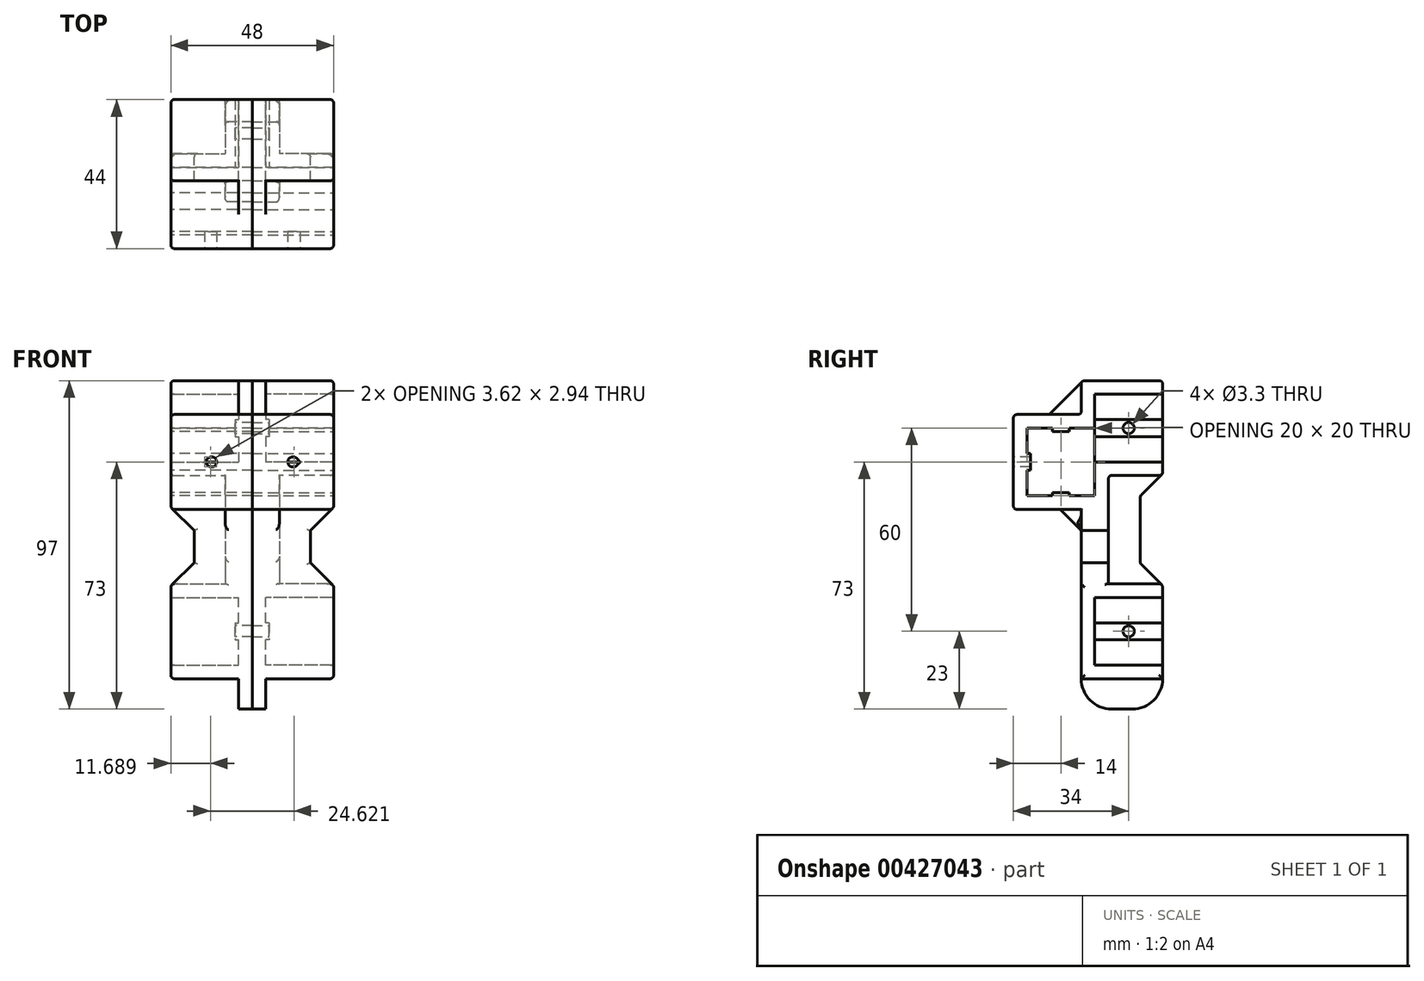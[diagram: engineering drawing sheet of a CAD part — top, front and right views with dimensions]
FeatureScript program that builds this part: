
annotation { "Feature Type Name" : "Feature", "Feature Type Description" : "" }
export const myFeature = defineFeature(function(context is Context, id is Id, definition is map)
    precondition{}
    {
        {
            var Q0;
            Q0=qCreatedBy(makeId("Right.planeOp"),FACE);
            var sketch = newSketch(context, id + "F0", { "sketchPlane" : qUnion([Q0])});
            skLineSegment(sketch, "E0", {"start": v(-23, 24) * mm, "end": v(-1, 24) * mm});
            skLineSegment(sketch, "E1", {"start": v(0, 23) * mm, "end": v(0, 20) * mm});
            skLineSegment(sketch, "E2", {"start": v(-1, -4) * mm, "end": v(-15, -4) * mm});
            skLineSegment(sketch, "E3", {"start": v(-16, -5) * mm, "end": v(-16, -14) * mm});
            skLineSegment(sketch, "E4", {"start": v(-16, -14) * mm, "end": v(-43, -14) * mm});
            skLineSegment(sketch, "E5", {"start": v(-44, -13) * mm, "end": v(-44, 13) * mm});
            skLineSegment(sketch, "E6", {"start": v(-43, 14) * mm, "end": v(-33.83, 14) * mm});
            skLineSegment(sketch, "E7", {"start": v(-24, 15) * mm, "end": v(-24, 23) * mm});
            skLineSegment(sketch, "E8", {"start": v(-23.7, 23.7) * mm, "end": v(-33.12, 14.3) * mm});
            skLineSegment(sketch, "E9", {"start": v(0, 20) * mm, "end": v(-20, 20) * mm});
            skLineSegment(sketch, "E10", {"start": v(-20, 20) * mm, "end": v(-20, 10) * mm});
            skLineSegment(sketch, "E11", {"start": v(-20, 10) * mm, "end": v(-27.5, 10) * mm});
            skLineSegment(sketch, "E12", {"start": v(-27.5, 10) * mm, "end": v(-27.5, 9) * mm});
            skLineSegment(sketch, "E13", {"start": v(-27.5, 9) * mm, "end": v(-32.5, 9) * mm});
            skLineSegment(sketch, "E14", {"start": v(-32.5, 9) * mm, "end": v(-32.5, 10) * mm});
            skLineSegment(sketch, "E15", {"start": v(-32.5, 10) * mm, "end": v(-40, 10) * mm});
            skLineSegment(sketch, "E16", {"start": v(-40, 10) * mm, "end": v(-40, 2.5) * mm});
            skLineSegment(sketch, "E17", {"start": v(-40, 2.5) * mm, "end": v(-39, 2.5) * mm});
            skLineSegment(sketch, "E18", {"start": v(-39, 2.5) * mm, "end": v(-39, -2.5) * mm});
            skLineSegment(sketch, "E19", {"start": v(-39, -2.5) * mm, "end": v(-40, -2.5) * mm});
            skLineSegment(sketch, "E20", {"start": v(-40, -2.5) * mm, "end": v(-40, -10) * mm});
            skLineSegment(sketch, "E21", {"start": v(-40, -10) * mm, "end": v(-32.5, -10) * mm});
            skLineSegment(sketch, "E22", {"start": v(-32.5, -10) * mm, "end": v(-32.5, -9) * mm});
            skLineSegment(sketch, "E23", {"start": v(-32.5, -9) * mm, "end": v(-27.5, -9) * mm});
            skLineSegment(sketch, "E24", {"start": v(-27.5, -9) * mm, "end": v(-27.5, -10) * mm});
            skLineSegment(sketch, "E25", {"start": v(-27.5, -10) * mm, "end": v(-20, -10) * mm});
            skLineSegment(sketch, "E26", {"start": v(-20, -10) * mm, "end": v(-20, 0) * mm});
            skLineSegment(sketch, "E27", {"start": v(-20, 0) * mm, "end": v(0, 0) * mm});
            skPoint(sketch, "E28.visualSharp", {"position": v(-44, 14) * mm});
            skArc(sketch, "E28.filletArc", {"start": v(-43, 14) * mm, "mid": v(-43.7, 13.7) * mm, "end": v(-44, 13) * mm});
            skPoint(sketch, "E29.visualSharp", {"position": v(-44, -14) * mm});
            skArc(sketch, "E29.filletArc", {"start": v(-44, -13) * mm, "mid": v(-43.7, -13.7) * mm, "end": v(-43, -14) * mm});
            skPoint(sketch, "E30.visualSharp", {"position": v(-16, -4) * mm});
            skArc(sketch, "E30.filletArc", {"start": v(-15, -4) * mm, "mid": v(-15.7, -4.3) * mm, "end": v(-16, -5) * mm});
            skPoint(sketch, "E31.visualSharp", {"position": v(0, 24) * mm});
            skArc(sketch, "E31.filletArc", {"start": v(0, 23) * mm, "mid": v(-0.3, 23.7) * mm, "end": v(-1, 24) * mm});
            skArc(sketch, "E32.filletArc", {"start": v(-23, 24) * mm, "mid": v(-23.7, 23.7) * mm, "end": v(-24, 23) * mm});
            skPoint(sketch, "E33.visualSharp", {"position": v(-24, 14) * mm});
            skArc(sketch, "E33.filletArc", {"start": v(-25, 14) * mm, "mid": v(-24.3, 14.3) * mm, "end": v(-24, 15) * mm});
            skLineSegment(sketch, "E34", {"start": v(-20, 0) * mm, "end": v(-20, 10) * mm});
            skLineSegment(sketch, "E35", {"start": v(0, 20) * mm, "end": v(0, 0) * mm});
            skArc(sketch, "E36.filletArc", {"start": v(-33.83, 14) * mm, "mid": v(-33.45, 14.08) * mm, "end": v(-33.12, 14.3) * mm});
            skLineSegment(sketch, "E37", {"start": v(-33.83, 14) * mm, "end": v(-25, 14) * mm});
            skLineSegment(sketch, "E38", {"start": v(-24, -64) * mm, "end": v(-24, -14) * mm});
            skLineSegment(sketch, "E39", {"start": v(0, -64) * mm, "end": v(0, -60) * mm});
            skLineSegment(sketch, "E40", {"start": v(0, -60) * mm, "end": v(-20, -60) * mm});
            skLineSegment(sketch, "E41", {"start": v(-20, -60) * mm, "end": v(-20, -40) * mm});
            skLineSegment(sketch, "E42", {"start": v(-20, -40) * mm, "end": v(0, -40) * mm});
            skLineSegment(sketch, "E43", {"start": v(0, -40) * mm, "end": v(0, -37) * mm});
            skLineSegment(sketch, "E44", {"start": v(-24, -64) * mm, "end": v(0, -64) * mm});
            skLineSegment(sketch, "E45", {"start": v(0, -60) * mm, "end": v(0, -40) * mm});
            skLineSegment(sketch, "E46", {"start": v(-1, -36) * mm, "end": v(-24, -36) * mm});
            skLineSegment(sketch, "E47", {"start": v(-16, -14) * mm, "end": v(-16, -36) * mm});
            skLineSegment(sketch, "E48", {"start": v(-30.27, -14) * mm, "end": v(-24, -20.27) * mm});
            skLineSegment(sketch, "E49", {"start": v(-6.56, -9.97) * mm, "end": v(-0.3, -3.7) * mm});
            skLineSegment(sketch, "E50", {"start": v(-6.56, -30.03) * mm, "end": v(-0.3, -36.3) * mm});
            skLineSegment(sketch, "E51", {"start": v(-6.56, -9.97) * mm, "end": v(-6.56, -30.03) * mm});
            skLineSegment(sketch, "E52", {"start": v(0, 0) * mm, "end": v(0, -3) * mm});
            skPoint(sketch, "E53.visualSharp", {"position": v(0, -4) * mm});
            skArc(sketch, "E53.filletArc", {"start": v(-1, -4) * mm, "mid": v(-0.3, -3.7) * mm, "end": v(0, -3) * mm});
            skPoint(sketch, "E54.visualSharp", {"position": v(0, -36) * mm});
            skArc(sketch, "E54.filletArc", {"start": v(0, -37) * mm, "mid": v(-0.3, -36.3) * mm, "end": v(-1, -36) * mm});
            skLineSegment(sketch, "E55", {"start": v(-24, -64) * mm, "end": v(-24, -64) * mm});
            skLineSegment(sketch, "E56", {"start": v(-15, -73) * mm, "end": v(-9, -73) * mm});
            skLineSegment(sketch, "E57", {"start": v(0, -64) * mm, "end": v(0, -64) * mm});
            skPoint(sketch, "E58.visualSharp", {"position": v(-24, -73) * mm});
            skArc(sketch, "E58.filletArc", {"start": v(-24, -64) * mm, "mid": v(-21.36, -70.36) * mm, "end": v(-15, -73) * mm});
            skPoint(sketch, "E59.visualSharp", {"position": v(0, -73) * mm});
            skArc(sketch, "E59.filletArc", {"start": v(-9, -73) * mm, "mid": v(-2.64, -70.36) * mm, "end": v(0, -64) * mm});
            skSolve(sketch);
        }
        {
            var Q0;
            Q0=makeQuery(id+"F0.imprint","IMPRINT",FACE,{"disambiguationData":[TD([[makeQuery(id+"F0.imprint","IMPRINT",EDGE,{"derivedFrom":sQuery(id+"F0.wireOp",EDGE,"E9")}),1.0]])]});
            var Q1;
            {var subQ1=sQuery(id+"F0.wireOp",EDGE,"E7");Q1=makeQuery(id+"F0.imprint","IMPRINT",FACE,{"disambiguationData":[TD([[makeQuery(id+"F0.imprint","IMPRINT",EDGE,{"derivedFrom":subQ1}),1.0]])]});}
            var Q2;
            {var subQ0=sQuery(id+"F0.wireOp",EDGE,"E0");Q2=makeQuery(id+"F0.imprint","IMPRINT",FACE,{"disambiguationData":[TD([[makeQuery(id+"F0.imprint","IMPRINT",EDGE,{"derivedFrom":subQ0}),-1.0]])]});}
            var Q3;
            Q3=makeQuery(id+"F0.imprint","IMPRINT",FACE,{"disambiguationData":[TD([[makeQuery(id+"F0.imprint","IMPRINT",EDGE,{"derivedFrom":sQuery(id+"F0.wireOp",EDGE,"E40")}),-1.0]])]});
            var Q4;
            {var subQ0=sQuery(id+"F0.wireOp",EDGE,"E38");Q4=makeQuery(id+"F0.imprint","IMPRINT",FACE,{"disambiguationData":[TD([[makeQuery(id+"F0.imprint","IMPRINT",EDGE,{"derivedFrom":subQ0}),-1.0]])]});}
            var Q5;
            Q5=makeQuery(id+"F0.imprint","IMPRINT",FACE,{"disambiguationData":[TD([[makeQuery(id+"F0.imprint","IMPRINT",EDGE,{"derivedFrom":sQuery(id+"F0.wireOp",EDGE,"E39")}),1.0]])]});
            var Q6;
            {var subQ3=sQuery(id+"F0.wireOp",EDGE,"E48");Q6=makeQuery(id+"F0.imprint","IMPRINT",FACE,{"disambiguationData":[TD([[makeQuery(id+"F0.imprint","IMPRINT",EDGE,{"derivedFrom":subQ3}),1.0]])]});}
            var Q7;
            {var subQ3=sQuery(id+"F0.wireOp",EDGE,"E50");Q7=makeQuery(id+"F0.imprint","IMPRINT",FACE,{"disambiguationData":[TD([[makeQuery(id+"F0.imprint","IMPRINT",EDGE,{"derivedFrom":subQ3}),-1.0]])]});}
            var Q8;
            {var subQ0=sQuery(id+"F0.wireOp",EDGE,"E30.filletArc");Q8=makeQuery(id+"F0.imprint","IMPRINT",FACE,{"disambiguationData":[TD([[makeQuery(id+"F0.imprint","IMPRINT",EDGE,{"derivedFrom":subQ0}),1.0]])]});}
            var Q9;
            Q9=makeQuery(id+"F0.imprint","IMPRINT",FACE,{"disambiguationData":[TD([[makeQuery(id+"F0.imprint","IMPRINT",EDGE,{"derivedFrom":sQuery(id+"F0.wireOp",EDGE,"E44")}),-1.0]])]});
            extrude(context, id + "F1", {"entities" : qUnion([Q0, Q1, Q2, Q3, Q4, Q5, Q6, Q7, Q8, Q9]), "oppositeDirection" : true, "depth" : 4 * mm});
        }
        {
            var Q0;
            Q0=makeQuery(id+"F0.imprint","IMPRINT",FACE,{"disambiguationData":[TD([[makeQuery(id+"F0.imprint","IMPRINT",EDGE,{"derivedFrom":sQuery(id+"F0.wireOp",EDGE,"E0")}),-1.0]])]});
            var Q1;
            Q1=makeQuery(id+"F0.imprint","IMPRINT",FACE,{"disambiguationData":[TD([[makeQuery(id+"F0.imprint","IMPRINT",EDGE,{"derivedFrom":sQuery(id+"F0.wireOp",EDGE,"E39")}),1.0]])]});
            extrude(context, id + "F2", {"entities" : qUnion([Q0, Q1]), "operationType" : NewBodyOperationType.ADD, "depth" : 20 * mm});
        }
        {
            var Q0;
            {var subQ0=sQuery(id+"F0.wireOp",EDGE,"E47");Q0=makeQuery(id+"F0.imprint","IMPRINT",FACE,{"disambiguationData":[TD([[makeQuery(id+"F0.imprint","IMPRINT",EDGE,{"derivedFrom":subQ0}),-1.0]])]});}
            var Q1;
            {var subQ3=sQuery(id+"F0.wireOp",EDGE,"E48");Q1=makeQuery(id+"F0.imprint","IMPRINT",FACE,{"disambiguationData":[TD([[makeQuery(id+"F0.imprint","IMPRINT",EDGE,{"derivedFrom":subQ3}),1.0]])]});}
            var Q2;
            {var subQ3=sQuery(id+"F0.wireOp",EDGE,"E50");Q2=makeQuery(id+"F0.imprint","IMPRINT",FACE,{"disambiguationData":[TD([[makeQuery(id+"F0.imprint","IMPRINT",EDGE,{"derivedFrom":subQ3}),-1.0]])]});}
            var Q3;
            {var subQ0=sQuery(id+"F0.wireOp",EDGE,"E30.filletArc");Q3=makeQuery(id+"F0.imprint","IMPRINT",FACE,{"disambiguationData":[TD([[makeQuery(id+"F0.imprint","IMPRINT",EDGE,{"derivedFrom":subQ0}),1.0]])]});}
            extrude(context, id + "F3", {"entities" : qUnion([Q0, Q1, Q2, Q3]), "operationType" : NewBodyOperationType.ADD, "depth" : 4 * mm});
        }
        {
            var Q0;
            {var subQ0=sQuery(id+"F0.wireOp",EDGE,"E44");var subQ1=sQuery(id+"F0.wireOp",EDGE,"E38");Q0=makeQuery(id+"F2.boolean.opBoolean","MERGE",EDGE,{"derivedFrom":[makeQuery(id+"F1.opExtrude","SWEPT_EDGE",EDGE,{"disambiguationData":[OSD([subQ1,subQ0])]}),makeQuery(id+"F2.opExtrude","SWEPT_EDGE",EDGE,{"disambiguationData":[OSD([subQ1,subQ0])]})]});}
            var Q1;
            Q1=makeQuery(id+"F2.opExtrude","CAP_EDGE",EDGE,{"disambiguationData":[OSD([sQuery(id+"F0.wireOp",EDGE,"E5")])],"isStart":false});
            var Q2;
            Q2=makeQuery(id+"F2.opExtrude","CAP_EDGE",EDGE,{"disambiguationData":[OSD([sQuery(id+"F0.wireOp",EDGE,"E38")])],"isStart":false});
            var Q3;
            Q3=makeQuery(id+"F2.opExtrude","CAP_EDGE",EDGE,{"disambiguationData":[OSD([sQuery(id+"F0.wireOp",EDGE,"E44")])],"isStart":false});
            var Q4;
            Q4=makeQuery(id+"F2.opExtrude","CAP_EDGE",EDGE,{"disambiguationData":[OSD([sQuery(id+"F0.wireOp",EDGE,"E39")])],"isStart":false});
            var Q5;
            Q5=makeQuery(id+"F2.opExtrude","CAP_EDGE",EDGE,{"disambiguationData":[OSD([sQuery(id+"F0.wireOp",EDGE,"E43")])],"isStart":false});
            var Q6;
            {var subQ0=sQuery(id+"F0.wireOp",EDGE,"E44");var subQ1=sQuery(id+"F0.wireOp",EDGE,"E38");Q6=makeQuery(id+"F2.boolean.opBoolean","MERGE",EDGE,{"derivedFrom":[makeQuery(id+"F1.opExtrude","SWEPT_EDGE",EDGE,{"disambiguationData":[OSD([subQ1,subQ0])]}),makeQuery(id+"F2.opExtrude","SWEPT_EDGE",EDGE,{"disambiguationData":[OSD([subQ1,subQ0])]})]});}
            var Q7;
            {var subQ0=sQuery(id+"F0.wireOp",EDGE,"E44");var subQ1=sQuery(id+"F0.wireOp",EDGE,"E39");Q7=makeQuery(id+"F2.boolean.opBoolean","MERGE",EDGE,{"derivedFrom":[makeQuery(id+"F1.opExtrude","SWEPT_EDGE",EDGE,{"disambiguationData":[OSD([subQ1,subQ0])]}),makeQuery(id+"F2.opExtrude","SWEPT_EDGE",EDGE,{"disambiguationData":[OSD([subQ1,subQ0])]})]});}
            var Q8;
            {var subQ0=sQuery(id+"F0.wireOp",EDGE,"E46");var subQ1=sQuery(id+"F0.wireOp",EDGE,"E43");Q8=makeQuery(id+"F2.boolean.opBoolean","MERGE",EDGE,{"derivedFrom":[makeQuery(id+"F1.opExtrude","SWEPT_EDGE",EDGE,{"disambiguationData":[OSD([subQ1,subQ0])]}),makeQuery(id+"F2.opExtrude","SWEPT_EDGE",EDGE,{"disambiguationData":[OSD([subQ1,subQ0])]})]});}
            var Q9;
            Q9=makeQuery(id+"F2.opExtrude","CAP_EDGE",EDGE,{"disambiguationData":[OSD([sQuery(id+"F0.wireOp",EDGE,"E46")])],"isStart":false});
            fillet(context, id + "F4", {"entities" : qUnion([Q0, Q1, Q2, Q3, Q4, Q5, Q6, Q7, Q8, Q9]), "radius" : 1 * mm, "tangentPropagation" : true, "allowEdgeOverflow" : false});
        }
        {
            var Q0;
            Q0=makeQuery(id+"F2.opExtrude","SWEPT_FACE",FACE,{"disambiguationData":[OSD([sQuery(id+"F0.wireOp",EDGE,"E3")])]});
            var sketch = newSketch(context, id + "F5", { "sketchPlane" : qUnion([Q0])});
            skLineSegment(sketch, "E60", {"start": v(-19.7, -36.3) * mm, "end": v(-13.15, -29.73) * mm});
            skLineSegment(sketch, "E61", {"start": v(-13.15, -29.73) * mm, "end": v(-13.15, -20.27) * mm});
            skLineSegment(sketch, "E62", {"start": v(-13.15, -20.27) * mm, "end": v(-19.7, -13.7) * mm});
            skPoint(sketch, "E63.0", {"position": v(-4, -20.27) * mm});
            skLineSegment(sketch, "E64", {"start": v(-4, -36) * mm, "end": v(-4, -14) * mm});
            skArc(sketch, "E65.0", {"start": v(-20, -13) * mm, "mid": v(-19.7, -13.7) * mm, "end": v(-19, -14) * mm});
            skLineSegment(sketch, "E66.0", {"start": v(-19, -14) * mm, "end": v(-4, -14) * mm});
            skArc(sketch, "E67.0", {"start": v(-19, -36) * mm, "mid": v(-19.7, -36.3) * mm, "end": v(-20, -37) * mm});
            skLineSegment(sketch, "E68", {"start": v(-19, -36) * mm, "end": v(-4, -36) * mm});
            skSolve(sketch);
        }
        {
            var Q0;
            {var subQ1=sQuery(id+"F5.wireOp",EDGE,"E60");Q0=makeQuery(id+"F5.imprint","IMPRINT",FACE,{"disambiguationData":[TD([[makeQuery(id+"F5.imprint","IMPRINT",EDGE,{"derivedFrom":subQ1}),-1.0]])]});}
            var Q1;
            {var subQ0=sQuery(id+"F0.wireOp",EDGE,"E38");Q1=makeQuery(id+"F3.boolean.opBoolean","MERGE",FACE,{"derivedFrom":[makeQuery(id+"F2.boolean.opBoolean","MERGE",FACE,{"derivedFrom":[makeQuery(id+"F1.opExtrude","SWEPT_FACE",FACE,{"disambiguationData":[OSD([subQ0])]}),makeQuery(id+"F2.opExtrude","SWEPT_FACE",FACE,{"disambiguationData":[OSD([subQ0])]})]}),makeQuery(id+"F3.opExtrude","SWEPT_FACE",FACE,{"disambiguationData":[OSD([subQ0])]})]});}
            extrude(context, id + "F6", {"entities" : qUnion([Q0]), "operationType" : NewBodyOperationType.ADD, "endBound" : BoundingType.UP_TO_SURFACE, "oppositeDirection" : true, "endBoundEntityFace" : qUnion([Q1]), "depth" : 25 * mm});
        }
        {
            var Q0;
            Q0=makeQuery(id+"F0.imprint","IMPRINT",FACE,{"disambiguationData":[TD([[makeQuery(id+"F0.imprint","IMPRINT",EDGE,{"derivedFrom":sQuery(id+"F0.wireOp",EDGE,"E9")}),1.0]])]});
            var sketch = newSketch(context, id + "F7", { "sketchPlane" : qUnion([Q0])});
            skPoint(sketch, "E69.0", {"position": v(-10, 20) * mm});
            skPoint(sketch, "E69.1", {"position": v(0, 10) * mm});
            skPoint(sketch, "E70", {"position": v(-10, 10) * mm});
            skLineSegment(sketch, "E71.bottom", {"start": v(0, 12.5) * mm, "end": v(-20, 12.5) * mm});
            skLineSegment(sketch, "E71.top", {"start": v(0, 7.5) * mm, "end": v(-20, 7.5) * mm});
            skLineSegment(sketch, "E71.left", {"start": v(0, 12.5) * mm, "end": v(0, 7.5) * mm});
            skLineSegment(sketch, "E71.right", {"start": v(-20, 12.5) * mm, "end": v(-20, 7.5) * mm});
            skLineSegment(sketch, "E72.bottom", {"start": v(0, -47.5) * mm, "end": v(-20, -47.5) * mm});
            skLineSegment(sketch, "E72.top", {"start": v(0, -52.5) * mm, "end": v(-20, -52.5) * mm});
            skLineSegment(sketch, "E72.left", {"start": v(0, -47.5) * mm, "end": v(0, -52.5) * mm});
            skLineSegment(sketch, "E72.right", {"start": v(-20, -47.5) * mm, "end": v(-20, -52.5) * mm});
            skPoint(sketch, "E73", {"position": v(0, -50) * mm});
            skPoint(sketch, "E74", {"position": v(-10, -50) * mm});
            skPoint(sketch, "E74.positionSnap0", {"position": v(-10, -47.5) * mm});
            skSolve(sketch);
        }
        {
            var Q0;
            {var subQ2=sQuery(id+"F7.wireOp",EDGE,"E71.bottom");Q0=makeQuery(id+"F7.imprint","IMPRINT",FACE,{"disambiguationData":[TD([[makeQuery(id+"F7.imprint","IMPRINT",EDGE,{"derivedFrom":subQ2}),1.0]])]});}
            var Q1;
            Q1=makeQuery(id+"F7.imprint","IMPRINT",FACE,{"disambiguationData":[TD([[makeQuery(id+"F7.imprint","IMPRINT",EDGE,{"derivedFrom":sQuery(id+"F7.wireOp",EDGE,"E72.bottom")}),1.0]])]});
            extrude(context, id + "F8", {"entities" : qUnion([Q0, Q1]), "operationType" : NewBodyOperationType.ADD, "depth" : 1 * mm});
        }
        {
            var Q0;
            {var subQ0=sQuery(id+"F0.wireOp",EDGE,"E38");Q0=makeQuery(id+"F6.opExtrude","TWEAK_EDGE",EDGE,{"derivedFrom":[makeQuery(id+"F3.boolean.opBoolean","MERGE",FACE,{"derivedFrom":[makeQuery(id+"F2.boolean.opBoolean","MERGE",FACE,{"derivedFrom":[makeQuery(id+"F1.opExtrude","SWEPT_FACE",FACE,{"disambiguationData":[OSD([subQ0])]}),makeQuery(id+"F2.opExtrude","SWEPT_FACE",FACE,{"disambiguationData":[OSD([subQ0])]})]}),makeQuery(id+"F3.opExtrude","SWEPT_FACE",FACE,{"disambiguationData":[OSD([subQ0])]})]}),makeQuery(id+"F5.imprint","IMPRINT",EDGE,{"derivedFrom":sQuery(id+"F5.wireOp",EDGE,"E62")})]});}
            var Q1;
            {var subQ0=sQuery(id+"F0.wireOp",EDGE,"E38");Q1=makeQuery(id+"F6.opExtrude","TWEAK_EDGE",EDGE,{"derivedFrom":[makeQuery(id+"F3.boolean.opBoolean","MERGE",FACE,{"derivedFrom":[makeQuery(id+"F2.boolean.opBoolean","MERGE",FACE,{"derivedFrom":[makeQuery(id+"F1.opExtrude","SWEPT_FACE",FACE,{"disambiguationData":[OSD([subQ0])]}),makeQuery(id+"F2.opExtrude","SWEPT_FACE",FACE,{"disambiguationData":[OSD([subQ0])]})]}),makeQuery(id+"F3.opExtrude","SWEPT_FACE",FACE,{"disambiguationData":[OSD([subQ0])]})]}),makeQuery(id+"F5.imprint","IMPRINT",EDGE,{"derivedFrom":sQuery(id+"F5.wireOp",EDGE,"E61")})]});}
            var Q2;
            {var subQ0=sQuery(id+"F0.wireOp",EDGE,"E38");Q2=makeQuery(id+"F6.opExtrude","TWEAK_EDGE",EDGE,{"derivedFrom":[makeQuery(id+"F3.boolean.opBoolean","MERGE",FACE,{"derivedFrom":[makeQuery(id+"F2.boolean.opBoolean","MERGE",FACE,{"derivedFrom":[makeQuery(id+"F1.opExtrude","SWEPT_FACE",FACE,{"disambiguationData":[OSD([subQ0])]}),makeQuery(id+"F2.opExtrude","SWEPT_FACE",FACE,{"disambiguationData":[OSD([subQ0])]})]}),makeQuery(id+"F3.opExtrude","SWEPT_FACE",FACE,{"disambiguationData":[OSD([subQ0])]})]}),makeQuery(id+"F5.imprint","IMPRINT",EDGE,{"derivedFrom":sQuery(id+"F5.wireOp",EDGE,"E60")})]});}
            var Q3;
            Q3=makeQuery(id+"F6.opExtrude","CAP_EDGE",EDGE,{"disambiguationData":[OSD([sQuery(id+"F5.wireOp",EDGE,"E60")])],"isStart":true});
            var Q4;
            Q4=makeQuery(id+"F6.opExtrude","CAP_EDGE",EDGE,{"disambiguationData":[OSD([sQuery(id+"F5.wireOp",EDGE,"E61")])],"isStart":true});
            var Q5;
            Q5=makeQuery(id+"F6.opExtrude","CAP_EDGE",EDGE,{"disambiguationData":[OSD([sQuery(id+"F5.wireOp",EDGE,"E62")])],"isStart":true});
            var Q6;
            {var subQ0=sQuery(id+"F0.wireOp",EDGE,"E51");var subQ1=sQuery(id+"F0.wireOp",EDGE,"E50");Q6=makeQuery(id+"F3.boolean.opBoolean","MERGE",EDGE,{"derivedFrom":[makeQuery(id+"F1.opExtrude","SWEPT_EDGE",EDGE,{"disambiguationData":[OSD([subQ1,subQ0])]}),makeQuery(id+"F3.opExtrude","SWEPT_EDGE",EDGE,{"disambiguationData":[OSD([subQ1,subQ0])]})]});}
            var Q7;
            {var subQ0=sQuery(id+"F0.wireOp",EDGE,"E51");var subQ1=sQuery(id+"F0.wireOp",EDGE,"E49");Q7=makeQuery(id+"F3.boolean.opBoolean","MERGE",EDGE,{"derivedFrom":[makeQuery(id+"F1.opExtrude","SWEPT_EDGE",EDGE,{"disambiguationData":[OSD([subQ1,subQ0])]}),makeQuery(id+"F3.opExtrude","SWEPT_EDGE",EDGE,{"disambiguationData":[OSD([subQ1,subQ0])]})]});}
            var Q8;
            Q8=makeQuery(id+"F3.opExtrude","CAP_EDGE",EDGE,{"disambiguationData":[OSD([sQuery(id+"F0.wireOp",EDGE,"E50")])],"isStart":false});
            var Q9;
            {var subQ0=sQuery(id+"F0.wireOp",EDGE,"E48");var subQ1=sQuery(id+"F0.wireOp",EDGE,"E4");Q9=makeQuery(id+"F3.boolean.opBoolean","MERGE",EDGE,{"derivedFrom":[makeQuery(id+"F1.opExtrude","SWEPT_EDGE",EDGE,{"disambiguationData":[OSD([subQ1,subQ0])]}),makeQuery(id+"F3.opExtrude","SWEPT_EDGE",EDGE,{"disambiguationData":[OSD([subQ1,subQ0])]})]});}
            var Q10;
            {var subQ0=sQuery(id+"F0.wireOp",EDGE,"E48");var subQ1=sQuery(id+"F0.wireOp",EDGE,"E38");Q10=makeQuery(id+"F3.boolean.opBoolean","MERGE",EDGE,{"derivedFrom":[makeQuery(id+"F1.opExtrude","SWEPT_EDGE",EDGE,{"disambiguationData":[OSD([subQ1,subQ0])]}),makeQuery(id+"F3.opExtrude","SWEPT_EDGE",EDGE,{"disambiguationData":[OSD([subQ1,subQ0])]})]});}
            var Q11;
            Q11=makeQuery(id+"F3.opExtrude","CAP_EDGE",EDGE,{"disambiguationData":[OSD([sQuery(id+"F0.wireOp",EDGE,"E48")])],"isStart":false});
            var Q12;
            {var subQ0=sQuery(id+"F0.wireOp",EDGE,"E38");Q12=makeQuery(id+"F6.opExtrude","TWEAK_EDGE",EDGE,{"derivedFrom":[makeQuery(id+"F3.boolean.opBoolean","MERGE",FACE,{"derivedFrom":[makeQuery(id+"F2.boolean.opBoolean","MERGE",FACE,{"derivedFrom":[makeQuery(id+"F1.opExtrude","SWEPT_FACE",FACE,{"disambiguationData":[OSD([subQ0])]}),makeQuery(id+"F2.opExtrude","SWEPT_FACE",FACE,{"disambiguationData":[OSD([subQ0])]})]}),makeQuery(id+"F3.opExtrude","SWEPT_FACE",FACE,{"disambiguationData":[OSD([subQ0])]})]}),makeQuery(id+"F5.imprint","IMPRINT",EDGE,{"derivedFrom":sQuery(id+"F5.wireOp",EDGE,"E66.0")})]});}
            var Q13;
            Q13=makeQuery(id+"F6.boolean.opBoolean","MERGE",EDGE,{"derivedFrom":[makeQuery(id+"F3.opExtrude","CAP_EDGE",EDGE,{"disambiguationData":[OSD([sQuery(id+"F0.wireOp",EDGE,"E3")])],"isStart":false}),makeQuery(id+"F6.opExtrude","CAP_EDGE",EDGE,{"disambiguationData":[OSD([sQuery(id+"F5.wireOp",EDGE,"E64")])],"isStart":true})]});
            var Q14;
            Q14=makeQuery(id+"F3.opExtrude","CAP_EDGE",EDGE,{"disambiguationData":[OSD([sQuery(id+"F0.wireOp",EDGE,"E46")])],"isStart":false});
            fillet(context, id + "F9", {"entities" : qUnion([Q0, Q1, Q2, Q3, Q4, Q5, Q6, Q7, Q8, Q9, Q10, Q11, Q12, Q13, Q14]), "radius" : 1 * mm, "tangentPropagation" : true, "allowEdgeOverflow" : false});
        }
        {
            var Q0;
            Q0=makeQuery(id+"F8.opExtrude","CAP_FACE",FACE,{"disambiguationData":[OSD([sQuery(id+"F7.wireOp",EDGE,"E71.bottom"),sQuery(id+"F7.wireOp",EDGE,"E71.top"),sQuery(id+"F7.wireOp",EDGE,"E71.left"),sQuery(id+"F7.wireOp",EDGE,"E71.right")])],"isStart":false});
            var sketch = newSketch(context, id + "F10", { "sketchPlane" : qUnion([Q0])});
            skPoint(sketch, "E75.0", {"position": v(-10, 10) * mm});
            skPoint(sketch, "E76.0", {"position": v(-10, -50) * mm});
            skSolve(sketch);
        }
        {
            var Q0;
            Q0=sQuery(id+"F10.wireOp",VERTEX,"E75.0");
            var Q1;
            Q1=sQuery(id+"F10.wireOp",VERTEX,"E76.0");
            var Q2;
            Q2=makeQuery(id+"F2.opExtrude","SWEPT_BODY",BODY,{"disambiguationData":[OSD([sQuery(id+"F0.wireOp",EDGE,"E0"),sQuery(id+"F0.wireOp",EDGE,"E1"),sQuery(id+"F0.wireOp",EDGE,"E2"),sQuery(id+"F0.wireOp",EDGE,"E3"),sQuery(id+"F0.wireOp",EDGE,"E4"),sQuery(id+"F0.wireOp",EDGE,"E5"),sQuery(id+"F0.wireOp",EDGE,"E6"),sQuery(id+"F0.wireOp",EDGE,"E7"),sQuery(id+"F0.wireOp",EDGE,"E9"),sQuery(id+"F0.wireOp",EDGE,"E10"),sQuery(id+"F0.wireOp",EDGE,"E11"),sQuery(id+"F0.wireOp",EDGE,"E12"),sQuery(id+"F0.wireOp",EDGE,"E13"),sQuery(id+"F0.wireOp",EDGE,"E14"),sQuery(id+"F0.wireOp",EDGE,"E15"),sQuery(id+"F0.wireOp",EDGE,"E16"),sQuery(id+"F0.wireOp",EDGE,"E17"),sQuery(id+"F0.wireOp",EDGE,"E18"),sQuery(id+"F0.wireOp",EDGE,"E19"),sQuery(id+"F0.wireOp",EDGE,"E20"),sQuery(id+"F0.wireOp",EDGE,"E21"),sQuery(id+"F0.wireOp",EDGE,"E22"),sQuery(id+"F0.wireOp",EDGE,"E23"),sQuery(id+"F0.wireOp",EDGE,"E24"),sQuery(id+"F0.wireOp",EDGE,"E25"),sQuery(id+"F0.wireOp",EDGE,"E26"),sQuery(id+"F0.wireOp",EDGE,"E27"),sQuery(id+"F0.wireOp",EDGE,"bd6adf50-98a7-4a62-9c91-a16b60b065ae.trimOffspring"),sQuery(id+"F0.wireOp",EDGE,"E28.filletArc"),sQuery(id+"F0.wireOp",EDGE,"E29.filletArc"),sQuery(id+"F0.wireOp",EDGE,"9b5b0097-369d-4008-899c-df93c46c1ec5.filletArc"),sQuery(id+"F0.wireOp",EDGE,"E30.filletArc"),sQuery(id+"F0.wireOp",EDGE,"5074b285-a29a-48ac-9bc0-d24b6333a393.filletArc"),sQuery(id+"F0.wireOp",EDGE,"E31.filletArc"),sQuery(id+"F0.wireOp",EDGE,"E32.filletArc"),sQuery(id+"F0.wireOp",EDGE,"E33.filletArc"),sQuery(id+"F0.wireOp",EDGE,"E37")])]});
            var Q3;
            Q3=makeQuery(id+"F1.opExtrude","SWEPT_BODY",BODY,{"disambiguationData":[OSD([sQuery(id+"F0.wireOp",EDGE,"E0"),sQuery(id+"F0.wireOp",EDGE,"E1"),sQuery(id+"F0.wireOp",EDGE,"E2"),sQuery(id+"F0.wireOp",EDGE,"E3"),sQuery(id+"F0.wireOp",EDGE,"E4"),sQuery(id+"F0.wireOp",EDGE,"E5"),sQuery(id+"F0.wireOp",EDGE,"E6"),sQuery(id+"F0.wireOp",EDGE,"E8"),sQuery(id+"F0.wireOp",EDGE,"E11"),sQuery(id+"F0.wireOp",EDGE,"E12"),sQuery(id+"F0.wireOp",EDGE,"E13"),sQuery(id+"F0.wireOp",EDGE,"E14"),sQuery(id+"F0.wireOp",EDGE,"E15"),sQuery(id+"F0.wireOp",EDGE,"E16"),sQuery(id+"F0.wireOp",EDGE,"E17"),sQuery(id+"F0.wireOp",EDGE,"E18"),sQuery(id+"F0.wireOp",EDGE,"E19"),sQuery(id+"F0.wireOp",EDGE,"E20"),sQuery(id+"F0.wireOp",EDGE,"E21"),sQuery(id+"F0.wireOp",EDGE,"E22"),sQuery(id+"F0.wireOp",EDGE,"E23"),sQuery(id+"F0.wireOp",EDGE,"E24"),sQuery(id+"F0.wireOp",EDGE,"E25"),sQuery(id+"F0.wireOp",EDGE,"E26"),sQuery(id+"F0.wireOp",EDGE,"bd6adf50-98a7-4a62-9c91-a16b60b065ae.trimOffspring"),sQuery(id+"F0.wireOp",EDGE,"E28.filletArc"),sQuery(id+"F0.wireOp",EDGE,"E29.filletArc"),sQuery(id+"F0.wireOp",EDGE,"9b5b0097-369d-4008-899c-df93c46c1ec5.filletArc"),sQuery(id+"F0.wireOp",EDGE,"E30.filletArc"),sQuery(id+"F0.wireOp",EDGE,"5074b285-a29a-48ac-9bc0-d24b6333a393.filletArc"),sQuery(id+"F0.wireOp",EDGE,"E31.filletArc"),sQuery(id+"F0.wireOp",EDGE,"E32.filletArc"),sQuery(id+"F0.wireOp",EDGE,"E34"),sQuery(id+"F0.wireOp",EDGE,"E35"),sQuery(id+"F0.wireOp",EDGE,"E36.filletArc"),sQuery(id+"F0.wireOp",EDGE,"E38"),sQuery(id+"F0.wireOp",EDGE,"E39"),sQuery(id+"F0.wireOp",EDGE,"E43"),sQuery(id+"F0.wireOp",EDGE,"njydVxAU-REJE-Qa92-eS4I-12LuDMoIE5Af"),sQuery(id+"F0.wireOp",EDGE,"m5lz31M7-Q2H7-C9Kg-khu1-IpoSL3evlFMB"),sQuery(id+"F0.wireOp",EDGE,"E44"),sQuery(id+"F0.wireOp",EDGE,"E45")])]});
            hole(context, id + "F11", {"style" : HoleStyle.SIMPLE, "endStyle" : HoleEndStyle.THROUGH, "standardTappedOrClearance" : lookupTablePath({ "standard" : "ISO", "fit" : "Normal", "size" : "M3", "type" : "Clearance" }), "standardBlindInLast" : lookupTablePath({ "fit" : "Standard", "standard" : "ISO", "size" : "M3", "type" : "Clearance" }), "holeDiameter" : 3.3 * mm, "isTappedThrough" : true, "tappedDepth" : 12 * mm, "tapClearance" : 3, "locations" : qUnion([Q0, Q1]), "scope" : qUnion([Q2, Q3])});
        }
        {
            var Q0;
            {var subQ0=sQuery(id+"F0.wireOp",EDGE,"E5");Q0=makeQuery(id+"F2.boolean.opBoolean","MERGE",FACE,{"derivedFrom":[makeQuery(id+"F1.opExtrude","SWEPT_FACE",FACE,{"disambiguationData":[OSD([subQ0])]}),makeQuery(id+"F2.opExtrude","SWEPT_FACE",FACE,{"disambiguationData":[OSD([subQ0])]})]});}
            var sketch = newSketch(context, id + "F12", { "sketchPlane" : qUnion([Q0])});
            skLineSegment(sketch, "E77.0.0", {"start": v(-4, 2.5) * mm, "end": v(20, 2.5) * mm});
            skLineSegment(sketch, "E77.0.1", {"start": v(20, 2.5) * mm, "end": v(20, -2.5) * mm});
            skLineSegment(sketch, "E77.0.2", {"start": v(20, -2.5) * mm, "end": v(-4, -2.5) * mm});
            skLineSegment(sketch, "E77.0.3", {"start": v(-4, -2.5) * mm, "end": v(-4, 2.5) * mm});
            skCircle(sketch, "E78", {"center": v(8, 0) * mm, "radius": 1.5 * mm});
            skPoint(sketch, "E78.centerSnap0", {"position": v(8, -2.5) * mm});
            skPoint(sketch, "E78.centerSnap1", {"position": v(20, 0) * mm});
            skLineSegment(sketch, "E79", {"start": v(10.12, 0) * mm, "end": v(9.06, -1.06) * mm});
            skLineSegment(sketch, "E80", {"start": v(10.12, 0) * mm, "end": v(9.06, 1.06) * mm});
            skSolve(sketch);
        }
        {
            var Q0;
            {var subQ0=sQuery(id+"F12.wireOp",EDGE,"E79");Q0=makeQuery(id+"F12.imprint","IMPRINT",FACE,{"disambiguationData":[TD([[makeQuery(id+"F12.imprint","IMPRINT",EDGE,{"derivedFrom":subQ0}),-1.0]])]});}
            var Q1;
            {var subQ0=sQuery(id+"F12.wireOp",EDGE,"E78");var subQ1=makeQuery(id+"F12.imprint","INTERSECT",VERTEX,{"derivedFrom":[subQ0,sQuery(id+"F12.wireOp",EDGE,"E79")]});Q1=makeQuery(id+"F12.imprint","IMPRINT",FACE,{"disambiguationData":[TD([[makeQuery(id+"F12.imprint","IMPRINT",EDGE,{"disambiguationData":[TD([[subQ1,1.0]])],"derivedFrom":subQ0}),1.0]])]});}
            extrude(context, id + "F13", {"entities" : qUnion([Q0, Q1]), "operationType" : NewBodyOperationType.REMOVE, "endBound" : BoundingType.UP_TO_NEXT, "oppositeDirection" : true, "depth" : 25 * mm});
        }
        {
            var Q0;
            Q0=makeQuery(id+"F2.opExtrude","SWEPT_BODY",BODY,{"disambiguationData":[OSD([sQuery(id+"F0.wireOp",EDGE,"E0"),sQuery(id+"F0.wireOp",EDGE,"E1"),sQuery(id+"F0.wireOp",EDGE,"E2"),sQuery(id+"F0.wireOp",EDGE,"E3"),sQuery(id+"F0.wireOp",EDGE,"E4"),sQuery(id+"F0.wireOp",EDGE,"E5"),sQuery(id+"F0.wireOp",EDGE,"E6"),sQuery(id+"F0.wireOp",EDGE,"E7"),sQuery(id+"F0.wireOp",EDGE,"E9"),sQuery(id+"F0.wireOp",EDGE,"E10"),sQuery(id+"F0.wireOp",EDGE,"E11"),sQuery(id+"F0.wireOp",EDGE,"E12"),sQuery(id+"F0.wireOp",EDGE,"E13"),sQuery(id+"F0.wireOp",EDGE,"E14"),sQuery(id+"F0.wireOp",EDGE,"E15"),sQuery(id+"F0.wireOp",EDGE,"E16"),sQuery(id+"F0.wireOp",EDGE,"E17"),sQuery(id+"F0.wireOp",EDGE,"E18"),sQuery(id+"F0.wireOp",EDGE,"E19"),sQuery(id+"F0.wireOp",EDGE,"E20"),sQuery(id+"F0.wireOp",EDGE,"E21"),sQuery(id+"F0.wireOp",EDGE,"E22"),sQuery(id+"F0.wireOp",EDGE,"E23"),sQuery(id+"F0.wireOp",EDGE,"E24"),sQuery(id+"F0.wireOp",EDGE,"E25"),sQuery(id+"F0.wireOp",EDGE,"E26"),sQuery(id+"F0.wireOp",EDGE,"E27"),sQuery(id+"F0.wireOp",EDGE,"bd6adf50-98a7-4a62-9c91-a16b60b065ae.trimOffspring"),sQuery(id+"F0.wireOp",EDGE,"E28.filletArc"),sQuery(id+"F0.wireOp",EDGE,"E29.filletArc"),sQuery(id+"F0.wireOp",EDGE,"9b5b0097-369d-4008-899c-df93c46c1ec5.filletArc"),sQuery(id+"F0.wireOp",EDGE,"E30.filletArc"),sQuery(id+"F0.wireOp",EDGE,"5074b285-a29a-48ac-9bc0-d24b6333a393.filletArc"),sQuery(id+"F0.wireOp",EDGE,"E31.filletArc"),sQuery(id+"F0.wireOp",EDGE,"E32.filletArc"),sQuery(id+"F0.wireOp",EDGE,"E33.filletArc"),sQuery(id+"F0.wireOp",EDGE,"E37")])]});
            var Q1;
            Q1=makeQuery(id+"F1.opExtrude","SWEPT_BODY",BODY,{"disambiguationData":[OSD([sQuery(id+"F0.wireOp",EDGE,"E0"),sQuery(id+"F0.wireOp",EDGE,"E1"),sQuery(id+"F0.wireOp",EDGE,"E2"),sQuery(id+"F0.wireOp",EDGE,"E3"),sQuery(id+"F0.wireOp",EDGE,"E4"),sQuery(id+"F0.wireOp",EDGE,"E5"),sQuery(id+"F0.wireOp",EDGE,"E6"),sQuery(id+"F0.wireOp",EDGE,"E8"),sQuery(id+"F0.wireOp",EDGE,"E11"),sQuery(id+"F0.wireOp",EDGE,"E12"),sQuery(id+"F0.wireOp",EDGE,"E13"),sQuery(id+"F0.wireOp",EDGE,"E14"),sQuery(id+"F0.wireOp",EDGE,"E15"),sQuery(id+"F0.wireOp",EDGE,"E16"),sQuery(id+"F0.wireOp",EDGE,"E17"),sQuery(id+"F0.wireOp",EDGE,"E18"),sQuery(id+"F0.wireOp",EDGE,"E19"),sQuery(id+"F0.wireOp",EDGE,"E20"),sQuery(id+"F0.wireOp",EDGE,"E21"),sQuery(id+"F0.wireOp",EDGE,"E22"),sQuery(id+"F0.wireOp",EDGE,"E23"),sQuery(id+"F0.wireOp",EDGE,"E24"),sQuery(id+"F0.wireOp",EDGE,"E25"),sQuery(id+"F0.wireOp",EDGE,"E26"),sQuery(id+"F0.wireOp",EDGE,"bd6adf50-98a7-4a62-9c91-a16b60b065ae.trimOffspring"),sQuery(id+"F0.wireOp",EDGE,"E28.filletArc"),sQuery(id+"F0.wireOp",EDGE,"E29.filletArc"),sQuery(id+"F0.wireOp",EDGE,"9b5b0097-369d-4008-899c-df93c46c1ec5.filletArc"),sQuery(id+"F0.wireOp",EDGE,"E30.filletArc"),sQuery(id+"F0.wireOp",EDGE,"5074b285-a29a-48ac-9bc0-d24b6333a393.filletArc"),sQuery(id+"F0.wireOp",EDGE,"E31.filletArc"),sQuery(id+"F0.wireOp",EDGE,"E32.filletArc"),sQuery(id+"F0.wireOp",EDGE,"E34"),sQuery(id+"F0.wireOp",EDGE,"E35"),sQuery(id+"F0.wireOp",EDGE,"E36.filletArc"),sQuery(id+"F0.wireOp",EDGE,"E38"),sQuery(id+"F0.wireOp",EDGE,"E39"),sQuery(id+"F0.wireOp",EDGE,"E43"),sQuery(id+"F0.wireOp",EDGE,"njydVxAU-REJE-Qa92-eS4I-12LuDMoIE5Af"),sQuery(id+"F0.wireOp",EDGE,"m5lz31M7-Q2H7-C9Kg-khu1-IpoSL3evlFMB"),sQuery(id+"F0.wireOp",EDGE,"E44"),sQuery(id+"F0.wireOp",EDGE,"E45")])]});
            var Q2;
            Q2=makeQuery(id+"F1.opExtrude","CAP_FACE",FACE,{"disambiguationData":[OSD([sQuery(id+"F0.wireOp",EDGE,"E0"),sQuery(id+"F0.wireOp",EDGE,"E1"),sQuery(id+"F0.wireOp",EDGE,"E2"),sQuery(id+"F0.wireOp",EDGE,"E3"),sQuery(id+"F0.wireOp",EDGE,"E4"),sQuery(id+"F0.wireOp",EDGE,"E5"),sQuery(id+"F0.wireOp",EDGE,"E6"),sQuery(id+"F0.wireOp",EDGE,"E8"),sQuery(id+"F0.wireOp",EDGE,"E11"),sQuery(id+"F0.wireOp",EDGE,"E12"),sQuery(id+"F0.wireOp",EDGE,"E13"),sQuery(id+"F0.wireOp",EDGE,"E14"),sQuery(id+"F0.wireOp",EDGE,"E15"),sQuery(id+"F0.wireOp",EDGE,"E16"),sQuery(id+"F0.wireOp",EDGE,"E17"),sQuery(id+"F0.wireOp",EDGE,"E18"),sQuery(id+"F0.wireOp",EDGE,"E19"),sQuery(id+"F0.wireOp",EDGE,"E20"),sQuery(id+"F0.wireOp",EDGE,"E21"),sQuery(id+"F0.wireOp",EDGE,"E22"),sQuery(id+"F0.wireOp",EDGE,"E23"),sQuery(id+"F0.wireOp",EDGE,"E24"),sQuery(id+"F0.wireOp",EDGE,"E25"),sQuery(id+"F0.wireOp",EDGE,"E26"),sQuery(id+"F0.wireOp",EDGE,"bd6adf50-98a7-4a62-9c91-a16b60b065ae.trimOffspring"),sQuery(id+"F0.wireOp",EDGE,"E28.filletArc"),sQuery(id+"F0.wireOp",EDGE,"E29.filletArc"),sQuery(id+"F0.wireOp",EDGE,"9b5b0097-369d-4008-899c-df93c46c1ec5.filletArc"),sQuery(id+"F0.wireOp",EDGE,"E30.filletArc"),sQuery(id+"F0.wireOp",EDGE,"5074b285-a29a-48ac-9bc0-d24b6333a393.filletArc"),sQuery(id+"F0.wireOp",EDGE,"E31.filletArc"),sQuery(id+"F0.wireOp",EDGE,"E32.filletArc"),sQuery(id+"F0.wireOp",EDGE,"E34"),sQuery(id+"F0.wireOp",EDGE,"E35"),sQuery(id+"F0.wireOp",EDGE,"E36.filletArc")])],"isStart":false});
            mirror(context, id + "F14", {"entities" : qUnion([Q0, Q1]), "mirrorPlane" : qUnion([Q2])});
        }
    });
